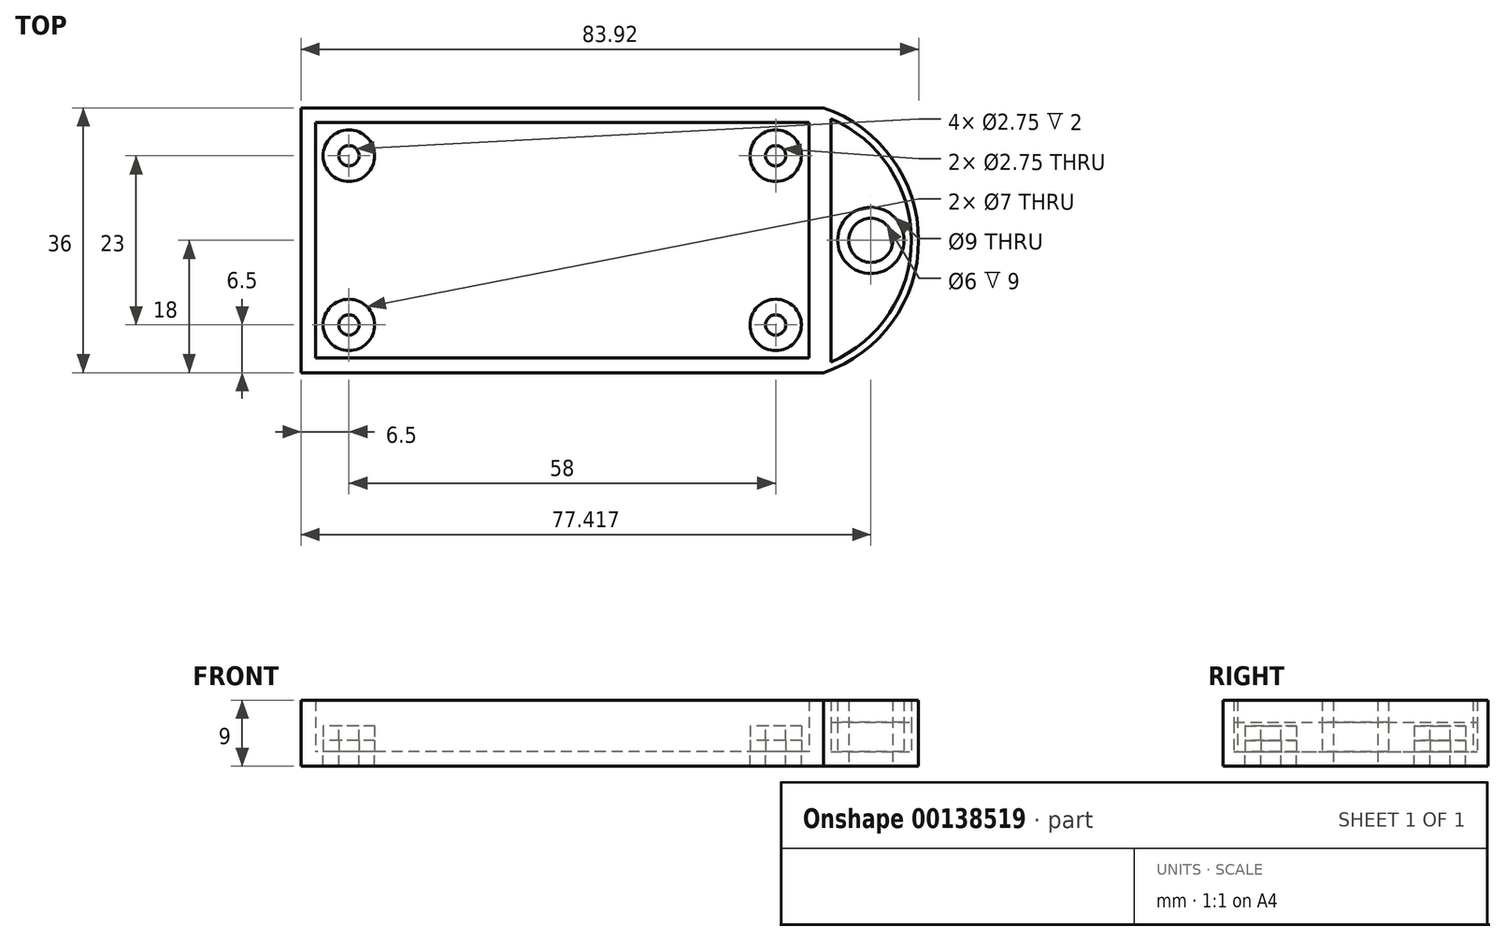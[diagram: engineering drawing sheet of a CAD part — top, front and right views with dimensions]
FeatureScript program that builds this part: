
annotation { "Feature Type Name" : "Feature", "Feature Type Description" : "" }
export const myFeature = defineFeature(function(context is Context, id is Id, definition is map)
    precondition{}
    {
        {
            var Q0;
            Q0=qCreatedBy(makeId("Top.planeOp"),FACE);
            var sketch = newSketch(context, id + "F0", { "sketchPlane" : qUnion([Q0])});
            skLineSegment(sketch, "E0.bottom", {"start": v(32.5, -15) * mm, "end": v(-32.5, -15) * mm});
            skLineSegment(sketch, "E0.top", {"start": v(32.5, 15) * mm, "end": v(-32.5, 15) * mm});
            skLineSegment(sketch, "E0.left", {"start": v(32.5, -15) * mm, "end": v(32.5, 15) * mm});
            skLineSegment(sketch, "E0.right", {"start": v(-32.5, -15) * mm, "end": v(-32.5, 15) * mm});
            skPoint(sketch, "E0.middle", {"position": v(0, 0) * mm});
            skCircle(sketch, "E1", {"center": v(29, 11.5) * mm, "radius": 1.38 * mm});
            skCircle(sketch, "E2.MirrorC", {"center": v(29, -11.5) * mm, "radius": 1.38 * mm});
            skCircle(sketch, "E3.MirrorC", {"center": v(-29, 11.5) * mm, "radius": 1.38 * mm});
            skCircle(sketch, "E4.MirrorC", {"center": v(-29, -11.5) * mm, "radius": 1.38 * mm});
            skLineSegment(sketch, "E5.0", {"start": v(33.5, 16) * mm, "end": v(-33.5, 16) * mm});
            skLineSegment(sketch, "E5.1", {"start": v(33.5, -16) * mm, "end": v(33.5, 16) * mm});
            skLineSegment(sketch, "E5.2", {"start": v(33.5, -16) * mm, "end": v(-33.5, -16) * mm});
            skLineSegment(sketch, "E5.3", {"start": v(-33.5, -16) * mm, "end": v(-33.5, 16) * mm});
            skLineSegment(sketch, "E6.0", {"start": v(35.5, 18) * mm, "end": v(-35.5, 18) * mm});
            skLineSegment(sketch, "E6.1", {"start": v(35.5, -18) * mm, "end": v(35.5, 18) * mm});
            skLineSegment(sketch, "E6.2", {"start": v(35.5, -18) * mm, "end": v(-35.5, -18) * mm});
            skLineSegment(sketch, "E6.3", {"start": v(-35.5, -18) * mm, "end": v(-35.5, 18) * mm});
            skCircle(sketch, "E7", {"center": v(41.92, 0) * mm, "radius": 3 * mm});
            skPoint(sketch, "E7.centerSnap0", {"position": v(35.5, 0) * mm});
            skCircle(sketch, "E8", {"center": v(41.92, 0) * mm, "radius": 4.5 * mm});
            skCircle(sketch, "E9", {"center": v(-29, -11.5) * mm, "radius": 3.5 * mm});
            skCircle(sketch, "E10", {"center": v(-29, 11.5) * mm, "radius": 3.5 * mm});
            skCircle(sketch, "E11", {"center": v(29, 11.5) * mm, "radius": 3.5 * mm});
            skCircle(sketch, "E12", {"center": v(29, -11.5) * mm, "radius": 3.5 * mm});
            skArc(sketch, "E13", {"start": v(35.5, -18) * mm, "mid": v(48.42, 0) * mm, "end": v(35.5, 18) * mm});
            skLineSegment(sketch, "E14.0", {"start": v(36.5, -16.55) * mm, "end": v(36.5, 16.55) * mm});
            skArc(sketch, "E14.1", {"start": v(36.5, -16.55) * mm, "mid": v(47.42, 0) * mm, "end": v(36.5, 16.55) * mm});
            skSolve(sketch);
        }
        {
            var Q0;
            Q0 = qSketchRegion(id + "F0", true);
            var Q1;
            Q1=makeQuery(id+"F0.imprint","IMPRINT",FACE,{"disambiguationData":[TD([[makeQuery(id+"F0.imprint","IMPRINT",EDGE,{"derivedFrom":sQuery(id+"F0.wireOp",EDGE,"E7")}),-1.0]])]});
            extrude(context, id + "F1", {"entities" : qUnion([Q0, Q1]), "depth" : 7 * mm});
        }
        {
            var Q0;
            Q0=makeQuery(id+"F0.imprint","IMPRINT",FACE,{"disambiguationData":[TD([[makeQuery(id+"F0.imprint","IMPRINT",EDGE,{"derivedFrom":sQuery(id+"F0.wireOp",EDGE,"E5.0")}),-1.0]])]});
            var Q1;
            Q1=makeQuery(id+"F0.imprint","IMPRINT",FACE,{"disambiguationData":[TD([[makeQuery(id+"F0.imprint","IMPRINT",EDGE,{"derivedFrom":sQuery(id+"F0.wireOp",EDGE,"E0.bottom")}),-1.0]])]});
            var Q2;
            Q2=makeQuery(id+"F0.imprint","IMPRINT",FACE,{"disambiguationData":[TD([[makeQuery(id+"F0.imprint","IMPRINT",EDGE,{"derivedFrom":sQuery(id+"F0.wireOp",EDGE,"E0.bottom")}),1.0]])]});
            var Q3;
            Q3=makeQuery(id+"F0.imprint","IMPRINT",FACE,{"disambiguationData":[TD([[makeQuery(id+"F0.imprint","IMPRINT",EDGE,{"derivedFrom":sQuery(id+"F0.wireOp",EDGE,"E2.MirrorC")}),-1.0]])]});
            var Q4;
            Q4=makeQuery(id+"F0.imprint","IMPRINT",FACE,{"disambiguationData":[TD([[makeQuery(id+"F0.imprint","IMPRINT",EDGE,{"derivedFrom":sQuery(id+"F0.wireOp",EDGE,"E1")}),1.0]])]});
            var Q5;
            Q5=makeQuery(id+"F0.imprint","IMPRINT",FACE,{"disambiguationData":[TD([[makeQuery(id+"F0.imprint","IMPRINT",EDGE,{"derivedFrom":sQuery(id+"F0.wireOp",EDGE,"E6.1")}),-1.0]])]});
            var Q6;
            Q6=makeQuery(id+"F0.imprint","IMPRINT",FACE,{"disambiguationData":[TD([[makeQuery(id+"F0.imprint","IMPRINT",EDGE,{"derivedFrom":sQuery(id+"F0.wireOp",EDGE,"E8")}),-1.0]])]});
            var Q7;
            Q7=makeQuery(id+"F0.imprint","IMPRINT",FACE,{"disambiguationData":[TD([[makeQuery(id+"F0.imprint","IMPRINT",EDGE,{"derivedFrom":sQuery(id+"F0.wireOp",EDGE,"E7")}),-1.0]])]});
            var Q8;
            Q8=makeQuery(id+"F0.imprint","IMPRINT",FACE,{"disambiguationData":[TD([[makeQuery(id+"F0.imprint","IMPRINT",EDGE,{"derivedFrom":sQuery(id+"F0.wireOp",EDGE,"E4.MirrorC")}),1.0]])]});
            var Q9;
            Q9=makeQuery(id+"F0.imprint","IMPRINT",FACE,{"disambiguationData":[TD([[makeQuery(id+"F0.imprint","IMPRINT",EDGE,{"derivedFrom":sQuery(id+"F0.wireOp",EDGE,"E3.MirrorC")}),-1.0]])]});
            var Q10;
            {var subQ5=sQuery(id+"F0.wireOp",EDGE,"E0.bottom");var subQ7=sQuery(id+"F0.wireOp",EDGE,"E12");var subQ15=makeQuery(id+"F0.imprint","INTERSECT",VERTEX,{"derivedFrom":[subQ5,subQ7]});Q10=makeQuery(id+"F0.imprint","IMPRINT",FACE,{"disambiguationData":[TD([[makeQuery(id+"F0.imprint","IMPRINT",EDGE,{"disambiguationData":[TD([[subQ15,-1.0]])],"derivedFrom":subQ5}),-1.0]])]});}
            var Q11;
            {var subQ0=sQuery(id+"F0.wireOp",EDGE,"E0.right");var subQ1=sQuery(id+"F0.wireOp",EDGE,"E0.top");var subQ2=makeQuery(id+"F0.imprint","INTERSECT",VERTEX,{"derivedFrom":[subQ1,subQ0]});Q11=makeQuery(id+"F0.imprint","IMPRINT",FACE,{"disambiguationData":[TD([[makeQuery(id+"F0.imprint","IMPRINT",EDGE,{"disambiguationData":[TD([[subQ2,1.0]])],"derivedFrom":subQ1}),1.0]])]});}
            var Q12;
            {var subQ0=sQuery(id+"F0.wireOp",EDGE,"E0.left");var subQ1=sQuery(id+"F0.wireOp",EDGE,"E0.top");var subQ2=makeQuery(id+"F0.imprint","INTERSECT",VERTEX,{"derivedFrom":[subQ1,subQ0]});Q12=makeQuery(id+"F0.imprint","IMPRINT",FACE,{"disambiguationData":[TD([[makeQuery(id+"F0.imprint","IMPRINT",EDGE,{"disambiguationData":[TD([[subQ2,-1.0]])],"derivedFrom":subQ1}),1.0]])]});}
            extrude(context, id + "F2", {"entities" : qUnion([Q0, Q1, Q2, Q3, Q4, Q5, Q6, Q7, Q8, Q9, Q10, Q11, Q12]), "operationType" : NewBodyOperationType.ADD, "oppositeDirection" : true, "depth" : 2 * mm});
        }
        {
            var Q0;
            Q0=makeQuery(id+"F0.imprint","IMPRINT",FACE,{"disambiguationData":[TD([[makeQuery(id+"F0.imprint","IMPRINT",EDGE,{"derivedFrom":sQuery(id+"F0.wireOp",EDGE,"E1")}),1.0]])]});
            var Q1;
            Q1=makeQuery(id+"F0.imprint","IMPRINT",FACE,{"disambiguationData":[TD([[makeQuery(id+"F0.imprint","IMPRINT",EDGE,{"derivedFrom":sQuery(id+"F0.wireOp",EDGE,"E2.MirrorC")}),-1.0]])]});
            var Q2;
            Q2=makeQuery(id+"F0.imprint","IMPRINT",FACE,{"disambiguationData":[TD([[makeQuery(id+"F0.imprint","IMPRINT",EDGE,{"derivedFrom":sQuery(id+"F0.wireOp",EDGE,"E4.MirrorC")}),1.0]])]});
            var Q3;
            Q3=makeQuery(id+"F0.imprint","IMPRINT",FACE,{"disambiguationData":[TD([[makeQuery(id+"F0.imprint","IMPRINT",EDGE,{"derivedFrom":sQuery(id+"F0.wireOp",EDGE,"E3.MirrorC")}),-1.0]])]});
            extrude(context, id + "F3", {"entities" : qUnion([Q0, Q1, Q2, Q3]), "operationType" : NewBodyOperationType.ADD, "depth" : 3.5 * mm});
        }
        {
            var Q0;
            Q0=makeQuery(id+"F0.imprint","IMPRINT",FACE,{"disambiguationData":[TD([[makeQuery(id+"F0.imprint","IMPRINT",EDGE,{"derivedFrom":sQuery(id+"F0.wireOp",EDGE,"E3.MirrorC")}),1.0]])]});
            var Q1;
            Q1=makeQuery(id+"F0.imprint","IMPRINT",FACE,{"disambiguationData":[TD([[makeQuery(id+"F0.imprint","IMPRINT",EDGE,{"derivedFrom":sQuery(id+"F0.wireOp",EDGE,"E1")}),-1.0]])]});
            var Q2;
            Q2=makeQuery(id+"F0.imprint","IMPRINT",FACE,{"disambiguationData":[TD([[makeQuery(id+"F0.imprint","IMPRINT",EDGE,{"derivedFrom":sQuery(id+"F0.wireOp",EDGE,"E2.MirrorC")}),1.0]])]});
            var Q3;
            Q3=makeQuery(id+"F0.imprint","IMPRINT",FACE,{"disambiguationData":[TD([[makeQuery(id+"F0.imprint","IMPRINT",EDGE,{"derivedFrom":sQuery(id+"F0.wireOp",EDGE,"E4.MirrorC")}),-1.0]])]});
            extrude(context, id + "F4", {"entities" : qUnion([Q0, Q1, Q2, Q3]), "depth" : 1.5 * mm});
        }
        {
            var Q0;
            Q0=makeQuery(id+"F0.imprint","IMPRINT",FACE,{"disambiguationData":[TD([[makeQuery(id+"F0.imprint","IMPRINT",EDGE,{"derivedFrom":sQuery(id+"F0.wireOp",EDGE,"E8")}),-1.0]])]});
            extrude(context, id + "F5", {"entities" : qUnion([Q0]), "depth" : 4 * mm});
        }
    });
